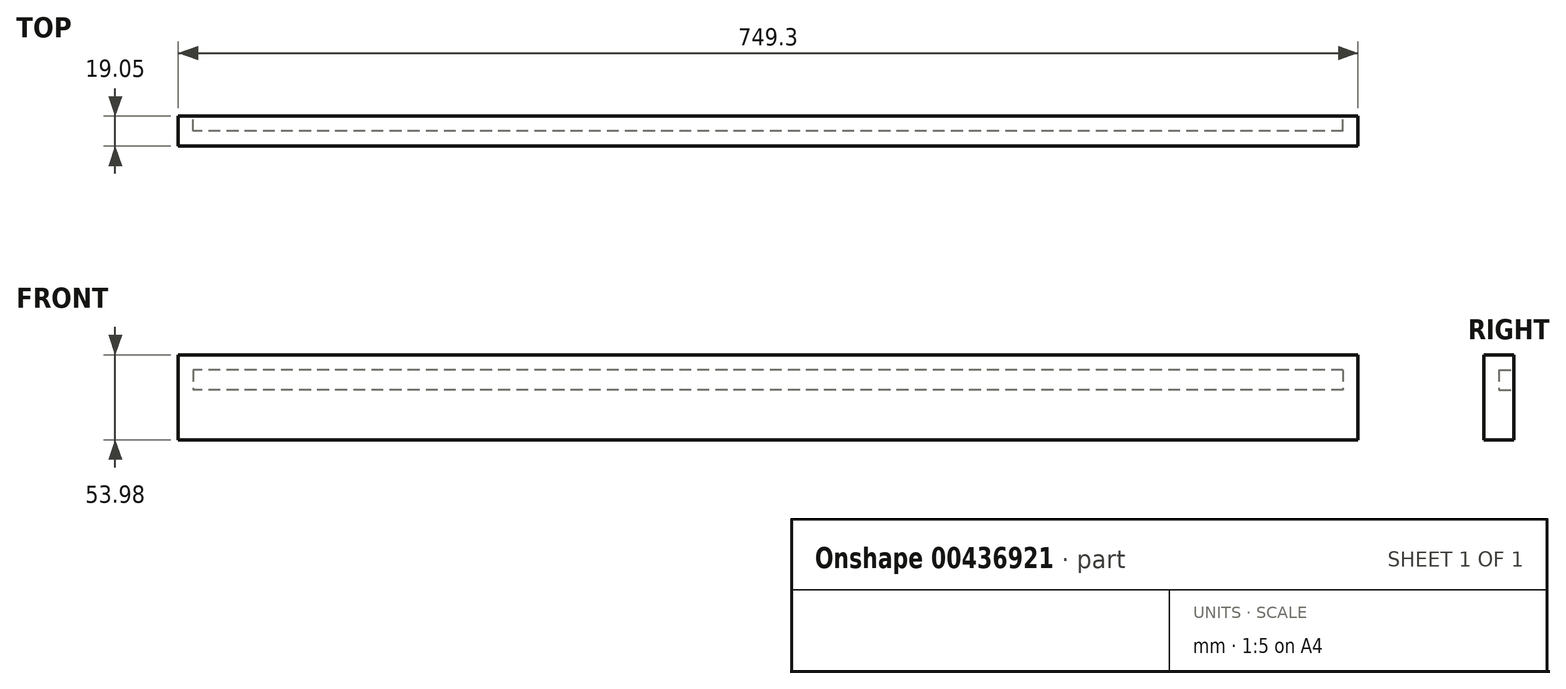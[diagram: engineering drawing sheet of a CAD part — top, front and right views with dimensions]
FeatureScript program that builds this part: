
annotation { "Feature Type Name" : "Feature", "Feature Type Description" : "" }
export const myFeature = defineFeature(function(context is Context, id is Id, definition is map)
    precondition{}
    {
        {
            var Q0;
            Q0=qCreatedBy(makeId("Front.planeOp"),FACE);
            var sketch = newSketch(context, id + "F0", { "sketchPlane" : qUnion([Q0])});
            skLineSegment(sketch, "E0.bottom", {"start": v(0, 0) * mm, "end": v(749.3, 0) * mm});
            skLineSegment(sketch, "E0.top", {"start": v(0, 53.98) * mm, "end": v(749.3, 53.98) * mm});
            skLineSegment(sketch, "E0.left", {"start": v(0, 0) * mm, "end": v(0, 53.98) * mm});
            skLineSegment(sketch, "E0.right", {"start": v(749.3, 0) * mm, "end": v(749.3, 53.98) * mm});
            skSolve(sketch);
        }
        {
            var Q0;
            Q0=makeQuery(id+"F0.imprint","IMPRINT",FACE,{"disambiguationData":[TD([[makeQuery(id+"F0.imprint","IMPRINT",EDGE,{"derivedFrom":sQuery(id+"F0.wireOp",EDGE,"E0.bottom")}),1.0]])]});
            extrude(context, id + "F1", {"entities" : qUnion([Q0]), "depth" : 19.05 * mm});
        }
        {
            var Q0;
            Q0=makeQuery(id+"F1.opExtrude","CAP_FACE",FACE,{"disambiguationData":[OSD([sQuery(id+"F0.wireOp",EDGE,"E0.bottom"),sQuery(id+"F0.wireOp",EDGE,"E0.top"),sQuery(id+"F0.wireOp",EDGE,"E0.left"),sQuery(id+"F0.wireOp",EDGE,"E0.right")])],"isStart":true});
            var sketch = newSketch(context, id + "F2", { "sketchPlane" : qUnion([Q0])});
            skLineSegment(sketch, "E1", {"start": v(-749.3, 53.98) * mm, "end": v(-749.3, 44.45) * mm});
            skLineSegment(sketch, "E2", {"start": v(-749.3, 44.45) * mm, "end": v(-739.78, 44.45) * mm});
            skLineSegment(sketch, "E3.bottom", {"start": v(-739.78, 44.45) * mm, "end": v(-9.53, 44.45) * mm});
            skLineSegment(sketch, "E3.top", {"start": v(-739.78, 31.75) * mm, "end": v(-9.53, 31.75) * mm});
            skLineSegment(sketch, "E3.left", {"start": v(-739.78, 44.45) * mm, "end": v(-739.78, 31.75) * mm});
            skLineSegment(sketch, "E3.right", {"start": v(-9.53, 44.45) * mm, "end": v(-9.53, 31.75) * mm});
            skSolve(sketch);
        }
        {
            var Q0;
            Q0=makeQuery(id+"F2.imprint","IMPRINT",FACE,{"disambiguationData":[TD([[makeQuery(id+"F2.imprint","IMPRINT",EDGE,{"derivedFrom":sQuery(id+"F2.wireOp",EDGE,"E3.bottom")}),-1.0]])]});
            extrude(context, id + "F3", {"entities" : qUnion([Q0]), "operationType" : NewBodyOperationType.REMOVE, "oppositeDirection" : true, "depth" : 9.52 * mm});
        }
    });
